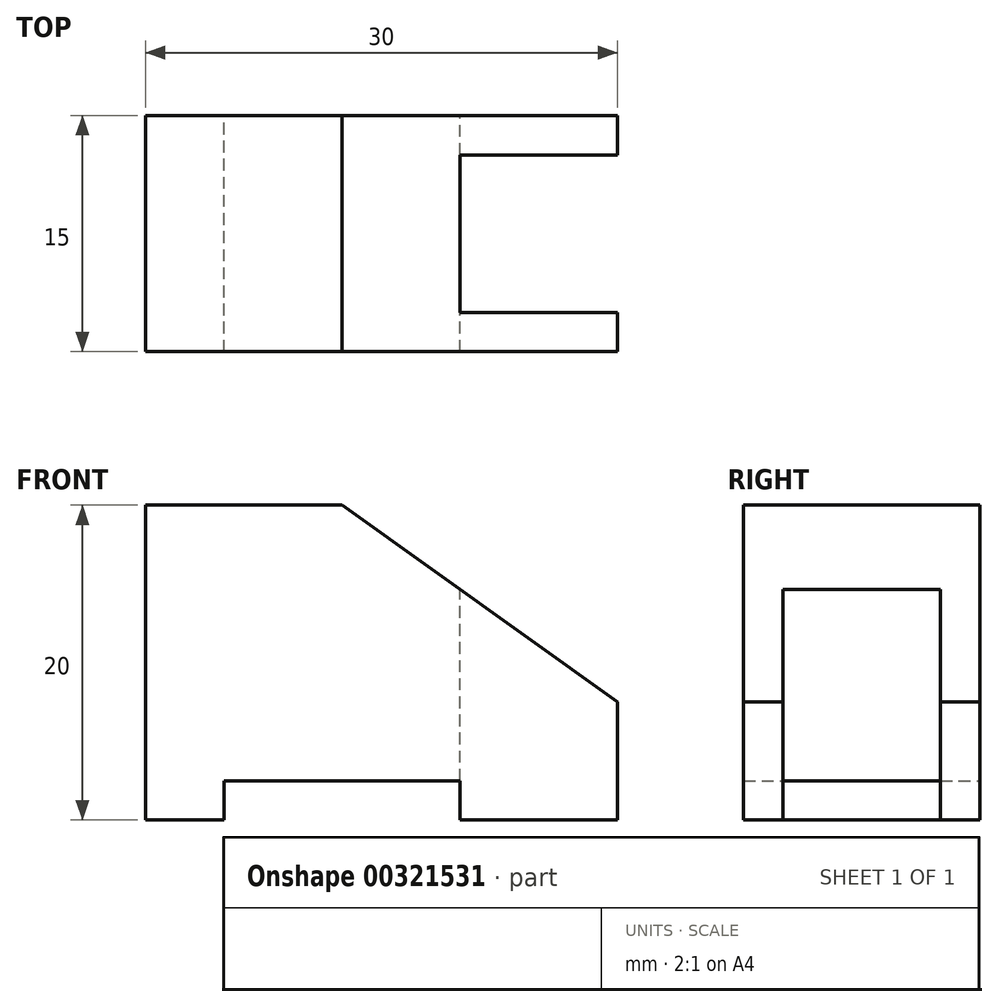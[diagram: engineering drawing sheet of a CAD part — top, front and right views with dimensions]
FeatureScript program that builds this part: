
annotation { "Feature Type Name" : "Feature", "Feature Type Description" : "" }
export const myFeature = defineFeature(function(context is Context, id is Id, definition is map)
    precondition{}
    {
        {
            var Q0;
            Q0=qCreatedBy(makeId("Front.planeOp"),FACE);
            var sketch = newSketch(context, id + "F0", { "sketchPlane" : qUnion([Q0])});
            skLineSegment(sketch, "E0", {"start": v(0, 0) * mm, "end": v(0, 20) * mm});
            skLineSegment(sketch, "E1", {"start": v(0, 20) * mm, "end": v(12.5, 20) * mm});
            skLineSegment(sketch, "E2", {"start": v(12.5, 20) * mm, "end": v(30, 7.5) * mm});
            skLineSegment(sketch, "E3", {"start": v(30, 7.5) * mm, "end": v(30, 0) * mm});
            skLineSegment(sketch, "E4", {"start": v(30, 0) * mm, "end": v(20, 0) * mm});
            skLineSegment(sketch, "E5", {"start": v(20, 0) * mm, "end": v(20, 2.5) * mm});
            skLineSegment(sketch, "E6", {"start": v(20, 2.5) * mm, "end": v(5, 2.5) * mm});
            skLineSegment(sketch, "E7", {"start": v(5, 2.5) * mm, "end": v(5, 0) * mm});
            skLineSegment(sketch, "E8", {"start": v(5, 0) * mm, "end": v(0, 0) * mm});
            skSolve(sketch);
        }
        {
            var Q0;
            Q0=makeQuery(id+"F0.imprint","IMPRINT",FACE,{"disambiguationData":[TD([[makeQuery(id+"F0.imprint","IMPRINT",EDGE,{"derivedFrom":sQuery(id+"F0.wireOp",EDGE,"E0")}),-1.0]])]});
            extrude(context, id + "F1", {"entities" : qUnion([Q0]), "depth" : 15 * mm});
        }
        {
            var Q0;
            Q0=makeQuery(id+"F1.opExtrude","SWEPT_FACE",FACE,{"disambiguationData":[OSD([sQuery(id+"F0.wireOp",EDGE,"E1")])]});
            var sketch = newSketch(context, id + "F2", { "sketchPlane" : qUnion([Q0])});
            skLineSegment(sketch, "E9", {"start": v(0, 0) * mm, "end": v(30, 0) * mm});
            skLineSegment(sketch, "E10", {"start": v(30, 0) * mm, "end": v(30, -15) * mm});
            skLineSegment(sketch, "E11", {"start": v(30, -15) * mm, "end": v(0, -15) * mm});
            skLineSegment(sketch, "E12", {"start": v(0, -15) * mm, "end": v(0, 0) * mm});
            skLineSegment(sketch, "E13", {"start": v(30, -2.5) * mm, "end": v(20, -2.5) * mm});
            skLineSegment(sketch, "E14", {"start": v(20, -2.5) * mm, "end": v(20, -12.5) * mm});
            skLineSegment(sketch, "E15", {"start": v(20, -12.5) * mm, "end": v(30, -12.5) * mm});
            skSolve(sketch);
        }
        {
            var Q0;
            {var subQ0=sQuery(id+"F2.wireOp",EDGE,"E13");Q0=makeQuery(id+"F2.imprint","IMPRINT",FACE,{"disambiguationData":[TD([[makeQuery(id+"F2.imprint","IMPRINT",EDGE,{"derivedFrom":subQ0}),1.0]])]});}
            extrude(context, id + "F3", {"entities" : qUnion([Q0]), "operationType" : NewBodyOperationType.REMOVE, "endBound" : BoundingType.THROUGH_ALL, "oppositeDirection" : true, "depth" : 25 * mm});
        }
    });
